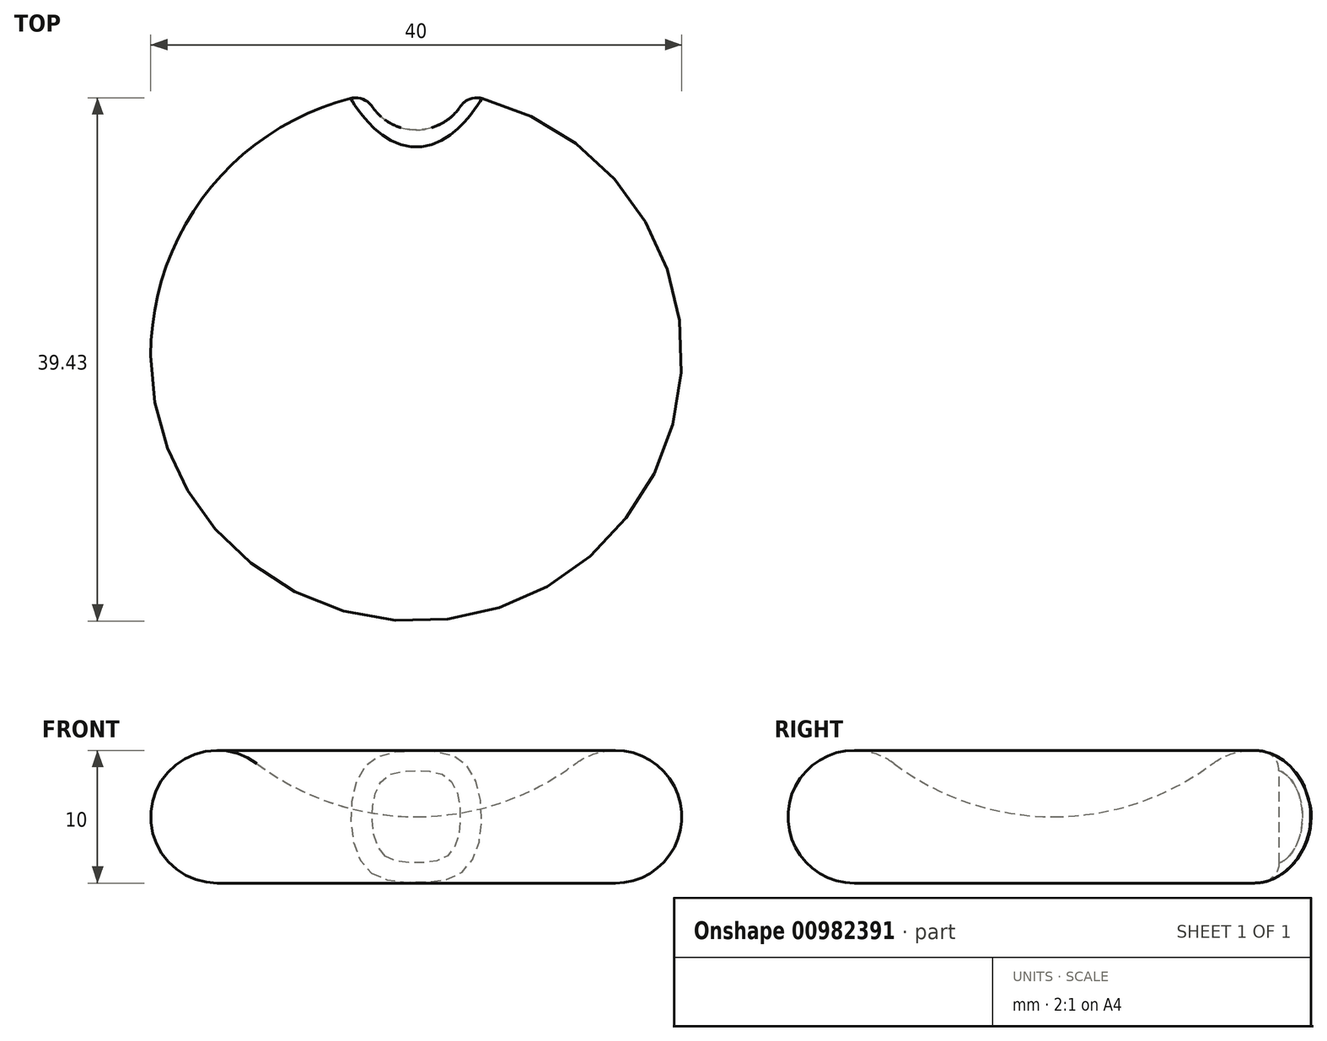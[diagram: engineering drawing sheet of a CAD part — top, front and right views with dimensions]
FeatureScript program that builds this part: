
annotation { "Feature Type Name" : "Feature", "Feature Type Description" : "" }
export const myFeature = defineFeature(function(context is Context, id is Id, definition is map)
    precondition{}
    {
        {
            var Q0;
            Q0=qCreatedBy(makeId("Front.planeOp"),FACE);
            var sketch = newSketch(context, id + "F0", { "sketchPlane" : qUnion([Q0])});
            skArc(sketch, "E0", {"start": v(-12, 9) * mm, "mid": v(-19.74, 6.58) * mm, "end": v(-15, 0) * mm});
            skArc(sketch, "E1", {"start": v(-12, 9) * mm, "mid": v(-6.32, 6.03) * mm, "end": v(0, 5) * mm});
            skLineSegment(sketch, "E2", {"start": v(-15, 0) * mm, "end": v(0, 0) * mm});
            skLineSegment(sketch, "E3", {"start": v(0, 0) * mm, "end": v(0, 5) * mm});
            skSolve(sketch);
        }
        {
            var Q0;
            Q0=makeQuery(id+"F0.imprint","IMPRINT",FACE,{"disambiguationData":[TD([[makeQuery(id+"F0.imprint","IMPRINT",EDGE,{"derivedFrom":sQuery(id+"F0.wireOp",EDGE,"E0")}),1.0]])]});
            var sketch = newSketch(context, id + "F1", { "sketchPlane" : qUnion([Q0])});
            skSolve(sketch);
        }
        {
            var Q0;
            Q0=makeQuery(id+"F0.imprint","IMPRINT",FACE,{"disambiguationData":[TD([[makeQuery(id+"F0.imprint","IMPRINT",EDGE,{"derivedFrom":sQuery(id+"F0.wireOp",EDGE,"E0")}),1.0]])]});
            var sketch = newSketch(context, id + "F2", { "sketchPlane" : qUnion([Q0])});
            skSolve(sketch);
        }
        {
            var Q0;
            Q0=makeQuery(id+"F2.imprint","IMPRINT",FACE,{"disambiguationData":[TD([[makeQuery(id+"F2.imprint","IMPRINT",EDGE,{"derivedFrom":makeQuery(id+"F0.imprint","IMPRINT",EDGE,{"derivedFrom":sQuery(id+"F0.wireOp",EDGE,"E0")})}),1.0]])]});
            var Q1;
            Q1=sQuery(id+"F0.wireOp",EDGE,"E3");
            revolve(context, id + "F3", {"surfaceOperationType" : NewSurfaceOperationType.NEW, "entities" : qUnion([Q0]), "axis" : qUnion([Q1]), "revolveType" : RevolveType.FULL});
        }
        {
            var Q0;
            Q0=qCreatedBy(makeId("Top.planeOp"),FACE);
            cPlane(context, id + "F4", {"entities" : qUnion([Q0]), "cplaneType" : CPlaneType.OFFSET, "offset" : 10 * mm, "width" : 150 * mm, "height" : 150 * mm});
        }
        {
            var Q0;
            Q0=qCreatedBy(id+"F4.planeOp",FACE);
            cPlane(context, id + "F5", {"entities" : qUnion([Q0]), "cplaneType" : CPlaneType.OFFSET, "offset" : 25 * mm, "width" : 150 * mm, "height" : 150 * mm});
        }
        {
            var Q0;
            Q0=qCreatedBy(id+"F5.planeOp",FACE);
            var sketch = newSketch(context, id + "F6", { "sketchPlane" : qUnion([Q0])});
            skCircle(sketch, "E4", {"center": v(0, 21) * mm, "radius": 4 * mm});
            skSolve(sketch);
        }
        {
            var Q0;
            Q0 = qSketchRegion(id + "F6", true);
            extrude(context, id + "F7", {"entities" : qUnion([Q0]), "operationType" : NewBodyOperationType.REMOVE, "oppositeDirection" : true, "depth" : 40.6 * mm, "offsetDistance" : 25 * mm});
        }
        {
            var Q0;
            Q0=makeQuery(id+"F7.boolean.opBoolean","INTERSECT",EDGE,{"derivedFrom":[makeQuery(id+"F3.opRevolve","SWEPT_FACE",FACE,{"disambiguationData":[OSD([sQuery(id+"F0.wireOp",EDGE,"E0")])]}),makeQuery(id+"F7.opExtrude","SWEPT_FACE",FACE,{"disambiguationData":[OSD([sQuery(id+"F6.wireOp",EDGE,"E4")])]})]});
            fillet(context, id + "F8", {"entities" : qUnion([Q0]), "radius" : 1.5 * mm, "tangentPropagation" : true, "allowEdgeOverflow" : false});
        }
    });
